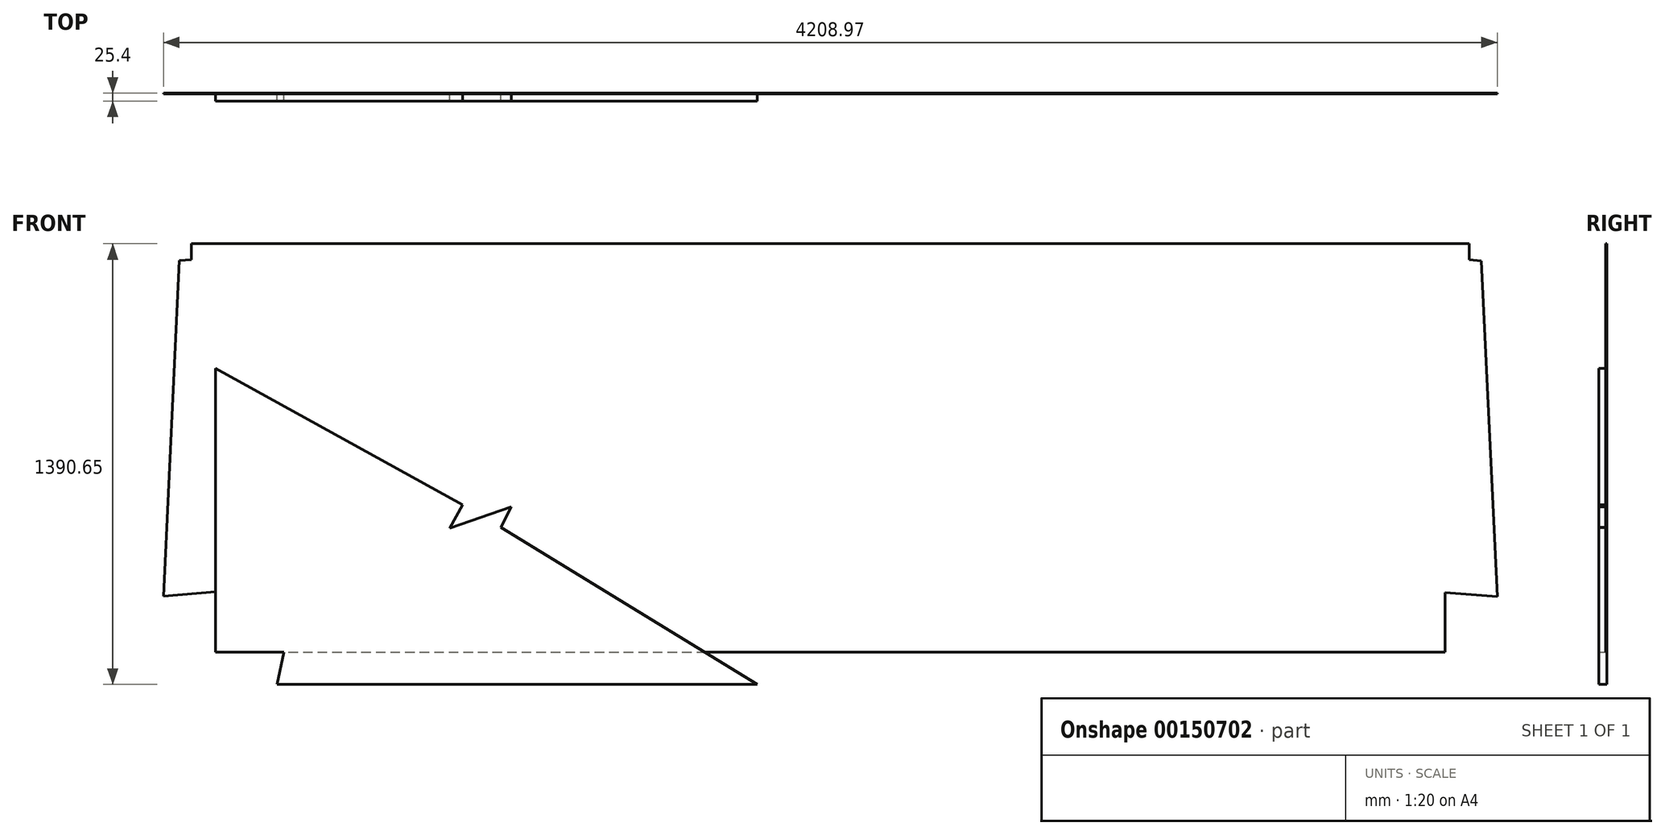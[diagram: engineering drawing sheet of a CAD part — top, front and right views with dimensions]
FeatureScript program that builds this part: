
annotation { "Feature Type Name" : "Feature", "Feature Type Description" : "" }
export const myFeature = defineFeature(function(context is Context, id is Id, definition is map)
    precondition{}
    {
        {
            var Q0;
            Q0=qCreatedBy(makeId("Front.planeOp"),FACE);
            var sketch = newSketch(context, id + "F0", { "sketchPlane" : qUnion([Q0])});
            skLineSegment(sketch, "E0", {"start": v(0, 0) * mm, "end": v(3879.85, 0) * mm});
            skLineSegment(sketch, "E1", {"start": v(0, 0) * mm, "end": v(0, 190.5) * mm});
            skLineSegment(sketch, "E2", {"start": v(3879.85, 0) * mm, "end": v(3879.85, 188.76) * mm});
            skLineSegment(sketch, "E3", {"start": v(-76.2, 1289.05) * mm, "end": v(3956.05, 1289.05) * mm});
            skLineSegment(sketch, "E4", {"start": v(3956.05, 1238.25) * mm, "end": v(3994, 1234.86) * mm});
            skLineSegment(sketch, "E5", {"start": v(3994, 1234.86) * mm, "end": v(4044.41, 175.47) * mm});
            skLineSegment(sketch, "E6", {"start": v(3956.05, 1238.25) * mm, "end": v(3956.05, 1289.05) * mm});
            skLineSegment(sketch, "E7", {"start": v(-76.2, 1238.25) * mm, "end": v(-114.26, 1236.57) * mm});
            skLineSegment(sketch, "E8", {"start": v(-114.26, 1236.57) * mm, "end": v(-164.56, 177.2) * mm});
            skLineSegment(sketch, "E9", {"start": v(-76.2, 1238.25) * mm, "end": v(-76.2, 1289.05) * mm});
            skLineSegment(sketch, "E10.0", {"start": v(0, 190.5) * mm, "end": v(-164.56, 177.2) * mm});
            skLineSegment(sketch, "E11.0", {"start": v(3879.85, 188.76) * mm, "end": v(4044.41, 175.47) * mm});
            skSolve(sketch);
        }
        {
            var Q0;
            Q0 = qSketchRegion(id + "F0", true);
            extrude(context, id + "F1", {"entities" : qUnion([Q0]), "depth" : 3.17 * mm});
        }
        {
            var Q0;
            Q0=qCreatedBy(makeId("Front.planeOp"),FACE);
            var sketch = newSketch(context, id + "F2", { "sketchPlane" : qUnion([Q0])});
            skLineSegment(sketch, "E12", {"start": v(0, 0) * mm, "end": v(215.9, 0) * mm});
            skLineSegment(sketch, "E13", {"start": v(0, 0) * mm, "end": v(0, 895.2) * mm});
            skLineSegment(sketch, "E14", {"start": v(193.68, -101.6) * mm, "end": v(1708.88, -101.6) * mm});
            skPoint(sketch, "E15.start.orphan", {"position": v(215.9, 0) * mm});
            skLineSegment(sketch, "E16", {"start": v(215.9, 0) * mm, "end": v(193.67, -101.6) * mm});
            skLineSegment(sketch, "E17", {"start": v(0, 895.2) * mm, "end": v(780.04, 465.6) * mm});
            skLineSegment(sketch, "E18", {"start": v(780.04, 465.6) * mm, "end": v(738.88, 390.86) * mm});
            skLineSegment(sketch, "E19", {"start": v(738.88, 390.86) * mm, "end": v(932.74, 459.35) * mm});
            skLineSegment(sketch, "E20", {"start": v(932.74, 459.35) * mm, "end": v(900.2, 394.26) * mm});
            skLineSegment(sketch, "E21", {"start": v(900.2, 394.26) * mm, "end": v(1708.88, -101.6) * mm});
            skSolve(sketch);
        }
        {
            var Q0;
            Q0 = qSketchRegion(id + "F2", true);
            extrude(context, id + "F3", {"entities" : qUnion([Q0]), "depth" : 25.4 * mm});
        }
    });
